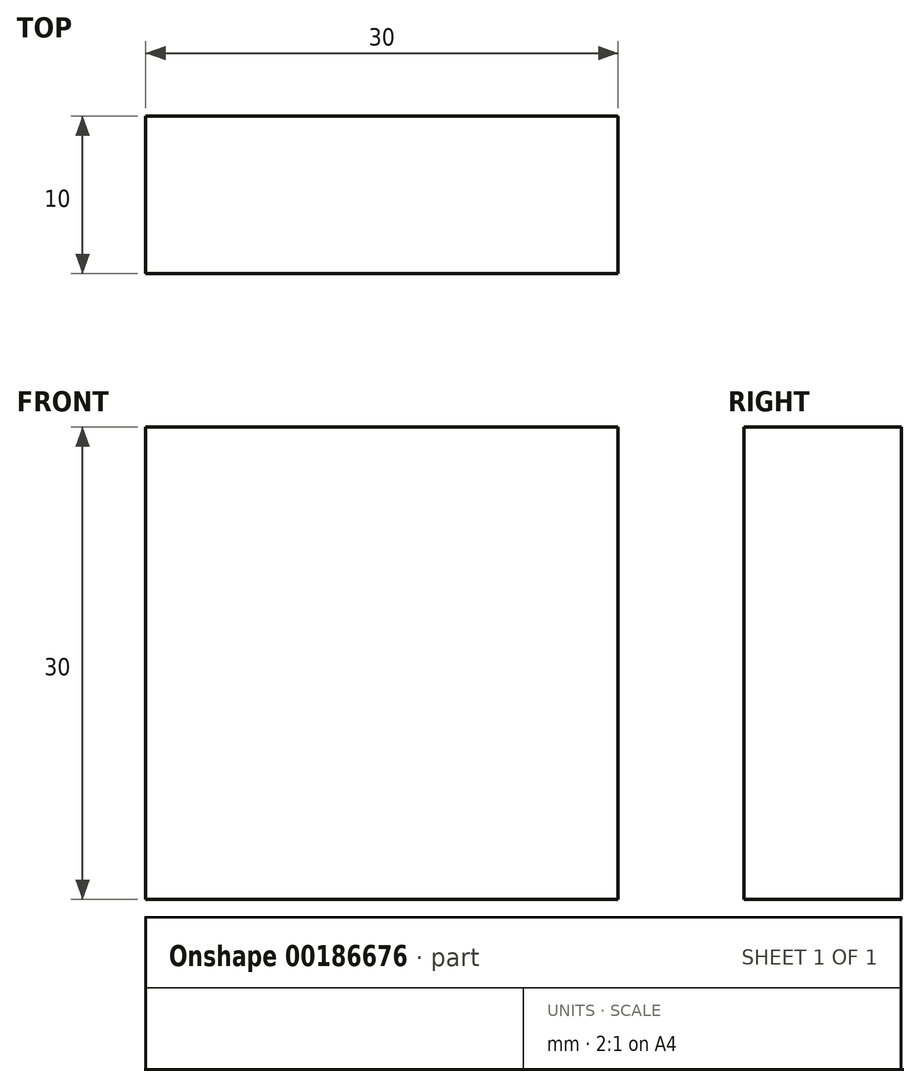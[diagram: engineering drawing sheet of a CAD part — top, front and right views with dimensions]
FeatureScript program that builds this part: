
annotation { "Feature Type Name" : "Feature", "Feature Type Description" : "" }
export const myFeature = defineFeature(function(context is Context, id is Id, definition is map)
    precondition{}
    {
        {
            var Q0;
            Q0=qCreatedBy(makeId("Top.planeOp"),FACE);
            var sketch = newSketch(context, id + "F0", { "sketchPlane" : qUnion([Q0])});
            skLineSegment(sketch, "E0.bottom", {"start": v(14.03, 7.32) * mm, "end": v(-15.97, 7.32) * mm});
            skLineSegment(sketch, "E0.top", {"start": v(14.03, -2.68) * mm, "end": v(-15.97, -2.68) * mm});
            skLineSegment(sketch, "E0.left", {"start": v(14.03, 7.32) * mm, "end": v(14.03, -2.68) * mm});
            skLineSegment(sketch, "E0.right", {"start": v(-15.97, 7.32) * mm, "end": v(-15.97, -2.68) * mm});
            skSolve(sketch);
        }
        {
            var Q0;
            Q0=makeQuery(id+"F0.imprint","IMPRINT",FACE,{"disambiguationData":[TD([[makeQuery(id+"F0.imprint","IMPRINT",EDGE,{"derivedFrom":sQuery(id+"F0.wireOp",EDGE,"E0.bottom")}),1.0]])]});
            extrude(context, id + "F1", {"entities" : qUnion([Q0]), "depth" : 30 * mm});
        }
    });
